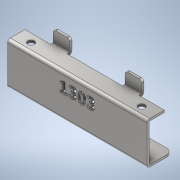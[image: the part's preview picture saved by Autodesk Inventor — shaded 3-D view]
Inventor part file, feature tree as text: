
AUTODESK INVENTOR PART (.ipt)
format: ipt  version: 2020 (Build 240168000, 168)  size: 544,256 bytes
history: native  units: mm
features: other x5, extrude x3, fillet x1, sketch x1, projected_geometry x1
ambient origin geometry x8: Origin, YZ Plane, XZ Plane, XY Plane, X Axis, Y Axis, Z Axis, Center Point
bodies: Body1 (feature_tree)
feature tree (11):
  other  "實體1"
  extrude  "擠出1"  Depth=126.0mm
  extrude  "擠出3"  Depth=21.3mm
  extrude  "擠出4"  Depth=33.0mm
  other  "折彎零件3"
  other  "折彎零件1"
  other  "折彎零件2"
  fillet  "圓角1"  Radius=14.0mm
  sketch  "草圖4"
  projected_geometry  "投影迴路1"
  other  "定義1"
